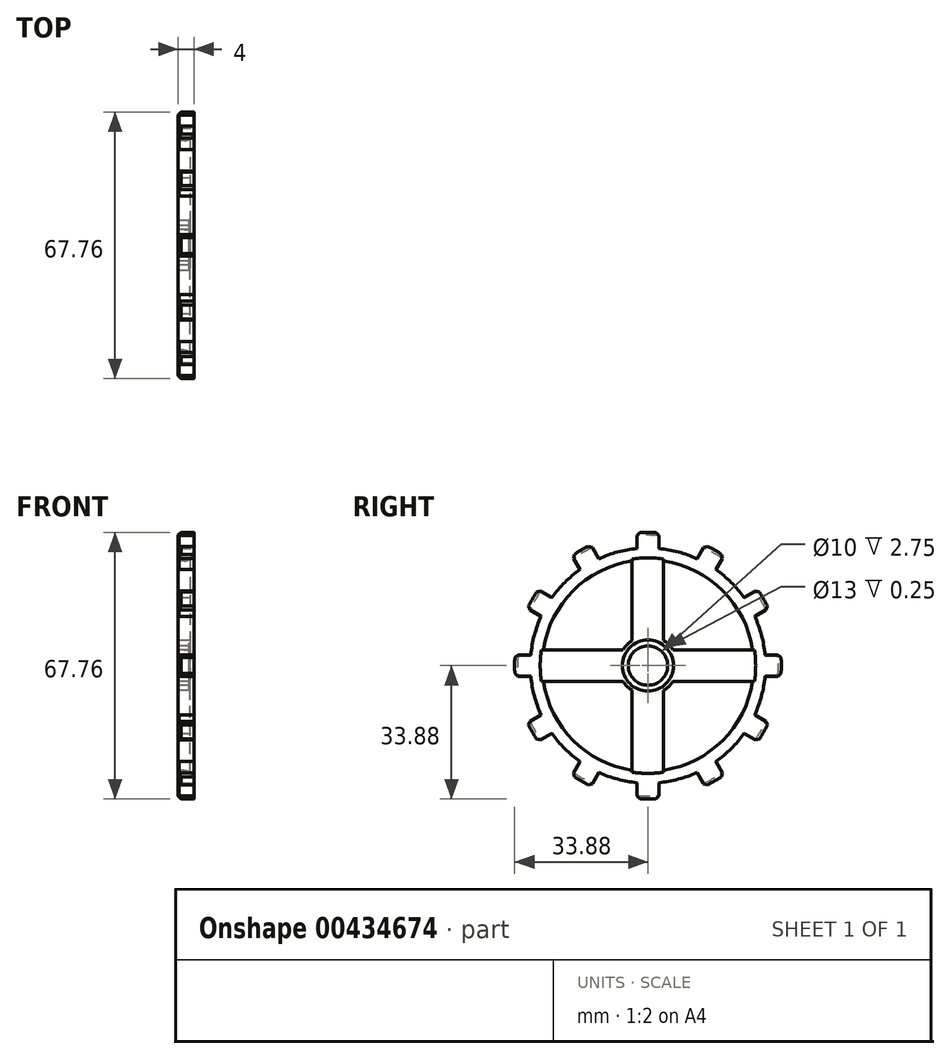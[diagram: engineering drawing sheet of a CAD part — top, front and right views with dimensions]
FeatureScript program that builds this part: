
annotation { "Feature Type Name" : "Feature", "Feature Type Description" : "" }
export const myFeature = defineFeature(function(context is Context, id is Id, definition is map)
    precondition{}
    {
        {
            assignVariable(context, id + "F0", {"name" : "Thickness", "anyValue" : 4});
        }
        {
            var Q0;
            Q0=qCreatedBy(makeId("Right.planeOp"),FACE);
            var sketch = newSketch(context, id + "F1", { "sketchPlane" : qUnion([Q0])});
            skLineSegment(sketch, "E0", {"start": v(-30, 0) * mm, "end": v(30, 0) * mm, "construction": true});
            skLineSegment(sketch, "E1", {"start": v(0, 30) * mm, "end": v(0, -30) * mm, "construction": true});
            skCircle(sketch, "E2", {"center": v(0, 0) * mm, "radius": 5 * mm});
            skCircle(sketch, "E3", {"center": v(0, 0) * mm, "radius": 6.5 * mm});
            skCircle(sketch, "E4", {"center": v(0, 0) * mm, "radius": 7.5 * mm});
            skSolve(sketch);
        }
        {
            var Q0;
            Q0=qCreatedBy(makeId("Right.planeOp"),FACE);
            var sketch = newSketch(context, id + "F2", { "sketchPlane" : qUnion([Q0])});
            skCircle(sketch, "E5", {"center": v(0, 0) * mm, "radius": 26.88 * mm});
            skCircle(sketch, "E6.0", {"center": v(0, 0) * mm, "radius": 29.88 * mm});
            skSolve(sketch);
        }
        {
            var Q0;
            Q0=qCreatedBy(makeId("Right.planeOp"),FACE);
            var sketch = newSketch(context, id + "F3", { "sketchPlane" : qUnion([Q0])});
            skCircle(sketch, "E7.0", {"center": v(0, 0) * mm, "radius": 26.88 * mm, "construction": true});
            skCircle(sketch, "E7.1", {"center": v(0, 0) * mm, "radius": 7.5 * mm, "construction": true});
            skLineSegment(sketch, "E7.2", {"start": v(-30, 0) * mm, "end": v(30, 0) * mm, "construction": true});
            skLineSegment(sketch, "E7.3", {"start": v(0, 30) * mm, "end": v(0, -30) * mm, "construction": true});
            skLineSegment(sketch, "E8", {"start": v(-4, 26.58) * mm, "end": v(-4, 6.34) * mm});
            skLineSegment(sketch, "E9.MirrorCS", {"start": v(4, 26.58) * mm, "end": v(4, 6.34) * mm});
            skArc(sketch, "E10", {"start": v(-4, 26.58) * mm, "mid": v(0, 26.88) * mm, "end": v(4, 26.58) * mm});
            skArc(sketch, "E11", {"start": v(-4, 6.34) * mm, "mid": v(0, 7.5) * mm, "end": v(4, 6.34) * mm});
            skArc(sketch, "E12.1.1", {"start": v(-6.34, -4) * mm, "mid": v(-7.5, 0) * mm, "end": v(-6.34, 4) * mm});
            skLineSegment(sketch, "E12.1.2", {"start": v(-26.58, -4) * mm, "end": v(-6.34, -4) * mm});
            skLineSegment(sketch, "E12.1.3", {"start": v(-26.58, 4) * mm, "end": v(-6.34, 4) * mm});
            skArc(sketch, "E12.1.4", {"start": v(-26.58, -4) * mm, "mid": v(-26.88, 0) * mm, "end": v(-26.58, 4) * mm});
            skArc(sketch, "E12.2.1", {"start": v(4, -6.34) * mm, "mid": v(0, -7.5) * mm, "end": v(-4, -6.34) * mm});
            skLineSegment(sketch, "E12.2.2", {"start": v(4, -26.58) * mm, "end": v(4, -6.34) * mm});
            skLineSegment(sketch, "E12.2.3", {"start": v(-4, -26.58) * mm, "end": v(-4, -6.34) * mm});
            skArc(sketch, "E12.2.4", {"start": v(4, -26.58) * mm, "mid": v(0, -26.88) * mm, "end": v(-4, -26.58) * mm});
            skArc(sketch, "E12.3.1", {"start": v(6.34, 4) * mm, "mid": v(7.5, 0) * mm, "end": v(6.34, -4) * mm});
            skLineSegment(sketch, "E12.3.2", {"start": v(26.58, 4) * mm, "end": v(6.34, 4) * mm});
            skLineSegment(sketch, "E12.3.3", {"start": v(26.58, -4) * mm, "end": v(6.34, -4) * mm});
            skArc(sketch, "E12.3.4", {"start": v(26.58, 4) * mm, "mid": v(26.88, 0) * mm, "end": v(26.58, -4) * mm});
            skSolve(sketch);
        }
        {
            var Q0;
            Q0=qCreatedBy(makeId("Right.planeOp"),FACE);
            var sketch = newSketch(context, id + "F4", { "sketchPlane" : qUnion([Q0])});
            skLineSegment(sketch, "E13.1", {"start": v(0, 30) * mm, "end": v(0, -30) * mm, "construction": true});
            skLineSegment(sketch, "E13.2", {"start": v(-30, 0) * mm, "end": v(30, 0) * mm, "construction": true});
            skLineSegment(sketch, "E14", {"start": v(-2.75, 29.75) * mm, "end": v(-2.75, 33.76) * mm});
            skLineSegment(sketch, "E15.MirrorCS", {"start": v(2.75, 29.75) * mm, "end": v(2.75, 33.76) * mm});
            skArc(sketch, "E16", {"start": v(2.75, 29.75) * mm, "mid": v(0, 29.88) * mm, "end": v(-2.75, 29.75) * mm});
            skArc(sketch, "E17.0", {"start": v(2.75, 33.76) * mm, "mid": v(0, 33.88) * mm, "end": v(-2.75, 33.76) * mm});
            skCircle(sketch, "E18.0", {"center": v(0, 0) * mm, "radius": 6.5 * mm});
            skArc(sketch, "E19.1.1", {"start": v(-12.5, 27.14) * mm, "mid": v(-14.94, 25.87) * mm, "end": v(-17.26, 24.39) * mm});
            skLineSegment(sketch, "E19.1.2", {"start": v(-17.26, 24.39) * mm, "end": v(-19.26, 27.86) * mm});
            skLineSegment(sketch, "E19.1.3", {"start": v(-12.5, 27.14) * mm, "end": v(-14.5, 30.61) * mm});
            skArc(sketch, "E19.1.4", {"start": v(-14.5, 30.61) * mm, "mid": v(-16.94, 29.34) * mm, "end": v(-19.26, 27.86) * mm});
            skArc(sketch, "E19.2.1", {"start": v(-24.39, 17.26) * mm, "mid": v(-25.87, 14.94) * mm, "end": v(-27.14, 12.5) * mm});
            skLineSegment(sketch, "E19.2.2", {"start": v(-27.14, 12.5) * mm, "end": v(-30.61, 14.5) * mm});
            skLineSegment(sketch, "E19.2.3", {"start": v(-24.39, 17.26) * mm, "end": v(-27.86, 19.26) * mm});
            skArc(sketch, "E19.2.4", {"start": v(-27.86, 19.26) * mm, "mid": v(-29.34, 16.94) * mm, "end": v(-30.61, 14.5) * mm});
            skArc(sketch, "E20.2.3.0", {"start": v(-29.75, 2.75) * mm, "mid": v(-29.88, 0) * mm, "end": v(-29.75, -2.75) * mm});
            skLineSegment(sketch, "E20.6.3.0", {"start": v(-29.75, -2.75) * mm, "end": v(-33.76, -2.75) * mm});
            skLineSegment(sketch, "E20.9.3.0", {"start": v(-29.75, 2.75) * mm, "end": v(-33.76, 2.75) * mm});
            skArc(sketch, "E20.12.3.0", {"start": v(-33.76, 2.75) * mm, "mid": v(-33.88, 0) * mm, "end": v(-33.76, -2.75) * mm});
            skArc(sketch, "E20.2.4.0", {"start": v(-27.14, -12.5) * mm, "mid": v(-25.87, -14.94) * mm, "end": v(-24.39, -17.26) * mm});
            skLineSegment(sketch, "E20.6.4.0", {"start": v(-24.39, -17.26) * mm, "end": v(-27.86, -19.26) * mm});
            skLineSegment(sketch, "E20.9.4.0", {"start": v(-27.14, -12.5) * mm, "end": v(-30.61, -14.5) * mm});
            skArc(sketch, "E20.12.4.0", {"start": v(-30.61, -14.5) * mm, "mid": v(-29.34, -16.94) * mm, "end": v(-27.86, -19.26) * mm});
            skArc(sketch, "E20.2.5.0", {"start": v(-17.26, -24.39) * mm, "mid": v(-14.94, -25.87) * mm, "end": v(-12.5, -27.14) * mm});
            skLineSegment(sketch, "E20.6.5.0", {"start": v(-12.5, -27.14) * mm, "end": v(-14.5, -30.61) * mm});
            skLineSegment(sketch, "E20.9.5.0", {"start": v(-17.26, -24.39) * mm, "end": v(-19.26, -27.86) * mm});
            skArc(sketch, "E20.12.5.0", {"start": v(-19.26, -27.86) * mm, "mid": v(-16.94, -29.34) * mm, "end": v(-14.5, -30.61) * mm});
            skArc(sketch, "E20.2.6.0", {"start": v(-2.75, -29.75) * mm, "mid": v(0, -29.88) * mm, "end": v(2.75, -29.75) * mm});
            skCircle(sketch, "E20.5.6.0", {"center": v(0, 0) * mm, "radius": 6.5 * mm, "construction": true});
            skLineSegment(sketch, "E20.6.6.0", {"start": v(2.75, -29.75) * mm, "end": v(2.75, -33.76) * mm});
            skLineSegment(sketch, "E20.9.6.0", {"start": v(-2.75, -29.75) * mm, "end": v(-2.75, -33.76) * mm});
            skArc(sketch, "E20.12.6.0", {"start": v(-2.75, -33.76) * mm, "mid": v(0, -33.88) * mm, "end": v(2.75, -33.76) * mm});
            skArc(sketch, "E20.2.7.0", {"start": v(12.5, -27.14) * mm, "mid": v(14.94, -25.87) * mm, "end": v(17.26, -24.39) * mm});
            skLineSegment(sketch, "E20.6.7.0", {"start": v(17.26, -24.39) * mm, "end": v(19.26, -27.86) * mm});
            skLineSegment(sketch, "E20.9.7.0", {"start": v(12.5, -27.14) * mm, "end": v(14.5, -30.61) * mm});
            skArc(sketch, "E20.12.7.0", {"start": v(14.5, -30.61) * mm, "mid": v(16.94, -29.34) * mm, "end": v(19.26, -27.86) * mm});
            skArc(sketch, "E20.2.8.0", {"start": v(24.39, -17.26) * mm, "mid": v(25.87, -14.94) * mm, "end": v(27.14, -12.5) * mm});
            skLineSegment(sketch, "E20.6.8.0", {"start": v(27.14, -12.5) * mm, "end": v(30.61, -14.5) * mm});
            skLineSegment(sketch, "E20.9.8.0", {"start": v(24.39, -17.26) * mm, "end": v(27.86, -19.26) * mm});
            skArc(sketch, "E20.12.8.0", {"start": v(27.86, -19.26) * mm, "mid": v(29.34, -16.94) * mm, "end": v(30.61, -14.5) * mm});
            skArc(sketch, "E20.2.9.0", {"start": v(29.75, -2.75) * mm, "mid": v(29.88, 0) * mm, "end": v(29.75, 2.75) * mm});
            skLineSegment(sketch, "E20.6.9.0", {"start": v(29.75, 2.75) * mm, "end": v(33.76, 2.75) * mm});
            skLineSegment(sketch, "E20.9.9.0", {"start": v(29.75, -2.75) * mm, "end": v(33.76, -2.75) * mm});
            skArc(sketch, "E20.12.9.0", {"start": v(33.76, -2.75) * mm, "mid": v(33.88, 0) * mm, "end": v(33.76, 2.75) * mm});
            skArc(sketch, "E20.2.10.0", {"start": v(27.14, 12.5) * mm, "mid": v(25.87, 14.94) * mm, "end": v(24.39, 17.26) * mm});
            skLineSegment(sketch, "E20.6.10.0", {"start": v(24.39, 17.26) * mm, "end": v(27.86, 19.26) * mm});
            skLineSegment(sketch, "E20.9.10.0", {"start": v(27.14, 12.5) * mm, "end": v(30.61, 14.5) * mm});
            skArc(sketch, "E20.12.10.0", {"start": v(30.61, 14.5) * mm, "mid": v(29.34, 16.94) * mm, "end": v(27.86, 19.26) * mm});
            skArc(sketch, "E20.2.11.0", {"start": v(17.26, 24.39) * mm, "mid": v(14.94, 25.87) * mm, "end": v(12.5, 27.14) * mm});
            skLineSegment(sketch, "E20.6.11.0", {"start": v(12.5, 27.14) * mm, "end": v(14.5, 30.61) * mm});
            skLineSegment(sketch, "E20.9.11.0", {"start": v(17.26, 24.39) * mm, "end": v(19.26, 27.86) * mm});
            skArc(sketch, "E20.12.11.0", {"start": v(19.26, 27.86) * mm, "mid": v(16.94, 29.34) * mm, "end": v(14.5, 30.61) * mm});
            skCircle(sketch, "E21.0", {"center": v(0, 0) * mm, "radius": 29.88 * mm, "construction": true});
            skSolve(sketch);
        }
        {
            var Q0;
            Q0=makeQuery(id+"F1.imprint","IMPRINT",FACE,{"disambiguationData":[TD([[makeQuery(id+"F1.imprint","IMPRINT",EDGE,{"derivedFrom":sQuery(id+"F1.wireOp",EDGE,"E2")}),-1.0]])]});
            extrude(context, id + "F5", {"entities" : qUnion([Q0]), "depth" : 2.5 * mm, "symmetric" : true});
        }
        {
            var Q0;
            Q0=makeQuery(id+"F1.imprint","IMPRINT",FACE,{"disambiguationData":[TD([[makeQuery(id+"F1.imprint","IMPRINT",EDGE,{"derivedFrom":sQuery(id+"F1.wireOp",EDGE,"E3")}),-1.0]])]});
            extrude(context, id + "F6", {"entities" : qUnion([Q0]), "operationType" : NewBodyOperationType.ADD, "depth" : 1.5 * mm});
        }
        {
            var Q0;
            Q0=makeQuery(id+"F1.imprint","IMPRINT",FACE,{"disambiguationData":[TD([[makeQuery(id+"F1.imprint","IMPRINT",EDGE,{"derivedFrom":sQuery(id+"F1.wireOp",EDGE,"E2")}),-1.0]])]});
            var Q1;
            Q1=makeQuery(id+"F1.imprint","IMPRINT",FACE,{"disambiguationData":[TD([[makeQuery(id+"F1.imprint","IMPRINT",EDGE,{"derivedFrom":sQuery(id+"F1.wireOp",EDGE,"E3")}),-1.0]])]});
            extrude(context, id + "F7", {"entities" : qUnion([Q0, Q1]), "operationType" : NewBodyOperationType.ADD, "oppositeDirection" : true, "depth" : 1.5 * mm});
        }
        {
            var Q0;
            Q0=qSketchRegion(id+"F3",true);
            extrude(context, id + "F8", {"entities" : qUnion([Q0]), "operationType" : NewBodyOperationType.ADD, "depth" : 3 * mm, "symmetric" : true});
        }
        {
            var Q0;
            Q0=makeQuery(id+"F2.imprint","IMPRINT",FACE,{"disambiguationData":[TD([[makeQuery(id+"F2.imprint","IMPRINT",EDGE,{"derivedFrom":sQuery(id+"F2.wireOp",EDGE,"E5")}),-1.0]])]});
            extrude(context, id + "F9", {"entities" : qUnion([Q0]), "operationType" : NewBodyOperationType.ADD, "depth" : (getVariable(context, 'Thickness') - 1.5) * mm, "hasSecondDirection" : true, "secondDirectionOppositeDirection" : true, "secondDirectionDepth" : 1.5 * mm});
        }
        {
            var Q0;
            Q0=makeQuery(id+"F4.imprint","IMPRINT",FACE,{"disambiguationData":[TD([[makeQuery(id+"F4.imprint","IMPRINT",EDGE,{"derivedFrom":sQuery(id+"F4.wireOp",EDGE,"E14")}),-1.0]])]});
            var Q1;
            Q1=makeQuery(id+"F4.imprint","IMPRINT",FACE,{"disambiguationData":[TD([[makeQuery(id+"F4.imprint","IMPRINT",EDGE,{"derivedFrom":sQuery(id+"F4.wireOp",EDGE,"E19.1.1")}),-1.0]])]});
            var Q2;
            Q2=makeQuery(id+"F4.imprint","IMPRINT",FACE,{"disambiguationData":[TD([[makeQuery(id+"F4.imprint","IMPRINT",EDGE,{"derivedFrom":sQuery(id+"F4.wireOp",EDGE,"E19.2.1")}),-1.0]])]});
            var Q3;
            Q3=makeQuery(id+"F4.imprint","IMPRINT",FACE,{"disambiguationData":[TD([[makeQuery(id+"F4.imprint","IMPRINT",EDGE,{"derivedFrom":sQuery(id+"F4.wireOp",EDGE,"E20.2.3.0")}),-1.0]])]});
            var Q4;
            Q4=makeQuery(id+"F4.imprint","IMPRINT",FACE,{"disambiguationData":[TD([[makeQuery(id+"F4.imprint","IMPRINT",EDGE,{"derivedFrom":sQuery(id+"F4.wireOp",EDGE,"E20.2.4.0")}),-1.0]])]});
            var Q5;
            Q5=makeQuery(id+"F4.imprint","IMPRINT",FACE,{"disambiguationData":[TD([[makeQuery(id+"F4.imprint","IMPRINT",EDGE,{"derivedFrom":sQuery(id+"F4.wireOp",EDGE,"E20.2.5.0")}),-1.0]])]});
            var Q6;
            Q6=makeQuery(id+"F4.imprint","IMPRINT",FACE,{"disambiguationData":[TD([[makeQuery(id+"F4.imprint","IMPRINT",EDGE,{"derivedFrom":sQuery(id+"F4.wireOp",EDGE,"E20.2.6.0")}),-1.0]])]});
            var Q7;
            Q7=makeQuery(id+"F4.imprint","IMPRINT",FACE,{"disambiguationData":[TD([[makeQuery(id+"F4.imprint","IMPRINT",EDGE,{"derivedFrom":sQuery(id+"F4.wireOp",EDGE,"E20.2.7.0")}),-1.0]])]});
            var Q8;
            Q8=makeQuery(id+"F4.imprint","IMPRINT",FACE,{"disambiguationData":[TD([[makeQuery(id+"F4.imprint","IMPRINT",EDGE,{"derivedFrom":sQuery(id+"F4.wireOp",EDGE,"E20.2.8.0")}),-1.0]])]});
            var Q9;
            Q9=makeQuery(id+"F4.imprint","IMPRINT",FACE,{"disambiguationData":[TD([[makeQuery(id+"F4.imprint","IMPRINT",EDGE,{"derivedFrom":sQuery(id+"F4.wireOp",EDGE,"E20.2.9.0")}),-1.0]])]});
            var Q10;
            Q10=makeQuery(id+"F4.imprint","IMPRINT",FACE,{"disambiguationData":[TD([[makeQuery(id+"F4.imprint","IMPRINT",EDGE,{"derivedFrom":sQuery(id+"F4.wireOp",EDGE,"E20.2.10.0")}),-1.0]])]});
            var Q11;
            Q11=makeQuery(id+"F4.imprint","IMPRINT",FACE,{"disambiguationData":[TD([[makeQuery(id+"F4.imprint","IMPRINT",EDGE,{"derivedFrom":sQuery(id+"F4.wireOp",EDGE,"E20.2.11.0")}),-1.0]])]});
            var Q12;
            Q12=makeQuery(id+"F9.opExtrude","CAP_FACE",FACE,{"disambiguationData":[OSD([sQuery(id+"F2.wireOp",EDGE,"E5"),sQuery(id+"F2.wireOp",EDGE,"E6.0")])],"isStart":false});
            extrude(context, id + "F10", {"entities" : qUnion([Q0, Q1, Q2, Q3, Q4, Q5, Q6, Q7, Q8, Q9, Q10, Q11]), "operationType" : NewBodyOperationType.ADD, "oppositeDirection" : true, "depth" : 1.5 * mm, "hasSecondDirection" : true, "secondDirectionBound" : BoundingType.UP_TO_SURFACE, "secondDirectionOppositeDirection" : false, "secondDirectionBoundEntityFace" : qUnion([Q12]), "secondDirectionDepth" : 25 * mm});
        }
        {
            var Q0;
            Q0=makeQuery(id+"F10.opExtrude","SWEPT_EDGE",EDGE,{"disambiguationData":[OSD([sQuery(id+"F4.wireOp",EDGE,"E20.9.9.0"),sQuery(id+"F4.wireOp",EDGE,"E20.12.9.0")])]});
            var Q1;
            Q1=makeQuery(id+"F10.opExtrude","SWEPT_EDGE",EDGE,{"disambiguationData":[OSD([sQuery(id+"F4.wireOp",EDGE,"E20.6.8.0"),sQuery(id+"F4.wireOp",EDGE,"E20.12.8.0")])]});
            var Q2;
            Q2=makeQuery(id+"F10.opExtrude","SWEPT_EDGE",EDGE,{"disambiguationData":[OSD([sQuery(id+"F4.wireOp",EDGE,"E20.9.8.0"),sQuery(id+"F4.wireOp",EDGE,"E20.12.8.0")])]});
            var Q3;
            Q3=makeQuery(id+"F10.opExtrude","SWEPT_EDGE",EDGE,{"disambiguationData":[OSD([sQuery(id+"F4.wireOp",EDGE,"E20.6.7.0"),sQuery(id+"F4.wireOp",EDGE,"E20.12.7.0")])]});
            var Q4;
            Q4=makeQuery(id+"F10.opExtrude","SWEPT_EDGE",EDGE,{"disambiguationData":[OSD([sQuery(id+"F4.wireOp",EDGE,"E20.9.7.0"),sQuery(id+"F4.wireOp",EDGE,"E20.12.7.0")])]});
            var Q5;
            Q5=makeQuery(id+"F10.opExtrude","SWEPT_EDGE",EDGE,{"disambiguationData":[OSD([sQuery(id+"F4.wireOp",EDGE,"E20.6.6.0"),sQuery(id+"F4.wireOp",EDGE,"E20.12.6.0")])]});
            var Q6;
            Q6=makeQuery(id+"F10.opExtrude","SWEPT_EDGE",EDGE,{"disambiguationData":[OSD([sQuery(id+"F4.wireOp",EDGE,"E20.9.6.0"),sQuery(id+"F4.wireOp",EDGE,"E20.12.6.0")])]});
            var Q7;
            Q7=makeQuery(id+"F10.opExtrude","SWEPT_EDGE",EDGE,{"disambiguationData":[OSD([sQuery(id+"F4.wireOp",EDGE,"E20.6.5.0"),sQuery(id+"F4.wireOp",EDGE,"E20.12.5.0")])]});
            var Q8;
            Q8=makeQuery(id+"F10.opExtrude","SWEPT_EDGE",EDGE,{"disambiguationData":[OSD([sQuery(id+"F4.wireOp",EDGE,"E20.9.5.0"),sQuery(id+"F4.wireOp",EDGE,"E20.12.5.0")])]});
            var Q9;
            Q9=makeQuery(id+"F10.opExtrude","SWEPT_EDGE",EDGE,{"disambiguationData":[OSD([sQuery(id+"F4.wireOp",EDGE,"E20.6.4.0"),sQuery(id+"F4.wireOp",EDGE,"E20.12.4.0")])]});
            var Q10;
            Q10=makeQuery(id+"F10.opExtrude","SWEPT_EDGE",EDGE,{"disambiguationData":[OSD([sQuery(id+"F4.wireOp",EDGE,"E20.9.4.0"),sQuery(id+"F4.wireOp",EDGE,"E20.12.4.0")])]});
            var Q11;
            Q11=makeQuery(id+"F10.opExtrude","SWEPT_EDGE",EDGE,{"disambiguationData":[OSD([sQuery(id+"F4.wireOp",EDGE,"E20.6.3.0"),sQuery(id+"F4.wireOp",EDGE,"E20.12.3.0")])]});
            var Q12;
            Q12=makeQuery(id+"F10.opExtrude","SWEPT_EDGE",EDGE,{"disambiguationData":[OSD([sQuery(id+"F4.wireOp",EDGE,"E20.9.3.0"),sQuery(id+"F4.wireOp",EDGE,"E20.12.3.0")])]});
            var Q13;
            Q13=makeQuery(id+"F10.opExtrude","SWEPT_EDGE",EDGE,{"disambiguationData":[OSD([sQuery(id+"F4.wireOp",EDGE,"E19.2.2"),sQuery(id+"F4.wireOp",EDGE,"E19.2.4")])]});
            var Q14;
            Q14=makeQuery(id+"F10.opExtrude","SWEPT_EDGE",EDGE,{"disambiguationData":[OSD([sQuery(id+"F4.wireOp",EDGE,"E19.1.2"),sQuery(id+"F4.wireOp",EDGE,"E19.1.4")])]});
            var Q15;
            Q15=makeQuery(id+"F10.opExtrude","SWEPT_EDGE",EDGE,{"disambiguationData":[OSD([sQuery(id+"F4.wireOp",EDGE,"E14"),sQuery(id+"F4.wireOp",EDGE,"E17.0")])]});
            var Q16;
            Q16=makeQuery(id+"F10.opExtrude","SWEPT_EDGE",EDGE,{"disambiguationData":[OSD([sQuery(id+"F4.wireOp",EDGE,"E20.9.11.0"),sQuery(id+"F4.wireOp",EDGE,"E20.12.11.0")])]});
            var Q17;
            Q17=makeQuery(id+"F10.opExtrude","SWEPT_EDGE",EDGE,{"disambiguationData":[OSD([sQuery(id+"F4.wireOp",EDGE,"E20.9.10.0"),sQuery(id+"F4.wireOp",EDGE,"E20.12.10.0")])]});
            var Q18;
            Q18=makeQuery(id+"F10.opExtrude","SWEPT_EDGE",EDGE,{"disambiguationData":[OSD([sQuery(id+"F4.wireOp",EDGE,"E20.6.9.0"),sQuery(id+"F4.wireOp",EDGE,"E20.12.9.0")])]});
            var Q19;
            Q19=makeQuery(id+"F10.opExtrude","SWEPT_EDGE",EDGE,{"disambiguationData":[OSD([sQuery(id+"F4.wireOp",EDGE,"E20.6.10.0"),sQuery(id+"F4.wireOp",EDGE,"E20.12.10.0")])]});
            var Q20;
            Q20=makeQuery(id+"F10.opExtrude","SWEPT_EDGE",EDGE,{"disambiguationData":[OSD([sQuery(id+"F4.wireOp",EDGE,"E20.6.11.0"),sQuery(id+"F4.wireOp",EDGE,"E20.12.11.0")])]});
            var Q21;
            Q21=makeQuery(id+"F10.opExtrude","SWEPT_EDGE",EDGE,{"disambiguationData":[OSD([sQuery(id+"F4.wireOp",EDGE,"E15.MirrorCS"),sQuery(id+"F4.wireOp",EDGE,"E17.0")])]});
            var Q22;
            Q22=makeQuery(id+"F10.opExtrude","SWEPT_EDGE",EDGE,{"disambiguationData":[OSD([sQuery(id+"F4.wireOp",EDGE,"E19.1.3"),sQuery(id+"F4.wireOp",EDGE,"E19.1.4")])]});
            var Q23;
            Q23=makeQuery(id+"F10.opExtrude","SWEPT_EDGE",EDGE,{"disambiguationData":[OSD([sQuery(id+"F4.wireOp",EDGE,"E19.2.3"),sQuery(id+"F4.wireOp",EDGE,"E19.2.4")])]});
            var Q24;
            Q24=makeQuery(id+"F10.opExtrude","TWEAK_EDGE",EDGE,{"derivedFrom":[makeQuery(id+"F9.opExtrude","CAP_FACE",FACE,{"disambiguationData":[OSD([sQuery(id+"F2.wireOp",EDGE,"E5"),sQuery(id+"F2.wireOp",EDGE,"E6.0")])],"isStart":false}),makeQuery(id+"F4.imprint","IMPRINT",EDGE,{"derivedFrom":sQuery(id+"F4.wireOp",EDGE,"E17.0")})]});
            var Q25;
            Q25=makeQuery(id+"F10.opExtrude","CAP_EDGE",EDGE,{"disambiguationData":[OSD([sQuery(id+"F4.wireOp",EDGE,"E17.0")])],"isStart":false});
            var Q26;
            Q26=makeQuery(id+"F10.opExtrude","CAP_EDGE",EDGE,{"disambiguationData":[OSD([sQuery(id+"F4.wireOp",EDGE,"E19.1.4")])],"isStart":false});
            var Q27;
            Q27=makeQuery(id+"F10.opExtrude","TWEAK_EDGE",EDGE,{"derivedFrom":[makeQuery(id+"F9.opExtrude","CAP_FACE",FACE,{"disambiguationData":[OSD([sQuery(id+"F2.wireOp",EDGE,"E5"),sQuery(id+"F2.wireOp",EDGE,"E6.0")])],"isStart":false}),makeQuery(id+"F4.imprint","IMPRINT",EDGE,{"derivedFrom":sQuery(id+"F4.wireOp",EDGE,"E19.1.4")})]});
            var Q28;
            Q28=makeQuery(id+"F10.opExtrude","CAP_EDGE",EDGE,{"disambiguationData":[OSD([sQuery(id+"F4.wireOp",EDGE,"E19.2.4")])],"isStart":false});
            var Q29;
            Q29=makeQuery(id+"F10.opExtrude","TWEAK_EDGE",EDGE,{"derivedFrom":[makeQuery(id+"F9.opExtrude","CAP_FACE",FACE,{"disambiguationData":[OSD([sQuery(id+"F2.wireOp",EDGE,"E5"),sQuery(id+"F2.wireOp",EDGE,"E6.0")])],"isStart":false}),makeQuery(id+"F4.imprint","IMPRINT",EDGE,{"derivedFrom":sQuery(id+"F4.wireOp",EDGE,"E19.2.4")})]});
            var Q30;
            Q30=makeQuery(id+"F10.opExtrude","TWEAK_EDGE",EDGE,{"derivedFrom":[makeQuery(id+"F9.opExtrude","CAP_FACE",FACE,{"disambiguationData":[OSD([sQuery(id+"F2.wireOp",EDGE,"E5"),sQuery(id+"F2.wireOp",EDGE,"E6.0")])],"isStart":false}),makeQuery(id+"F4.imprint","IMPRINT",EDGE,{"derivedFrom":sQuery(id+"F4.wireOp",EDGE,"E20.12.3.0")})]});
            var Q31;
            Q31=makeQuery(id+"F10.opExtrude","CAP_EDGE",EDGE,{"disambiguationData":[OSD([sQuery(id+"F4.wireOp",EDGE,"E20.12.3.0")])],"isStart":false});
            var Q32;
            Q32=makeQuery(id+"F10.opExtrude","TWEAK_EDGE",EDGE,{"derivedFrom":[makeQuery(id+"F9.opExtrude","CAP_FACE",FACE,{"disambiguationData":[OSD([sQuery(id+"F2.wireOp",EDGE,"E5"),sQuery(id+"F2.wireOp",EDGE,"E6.0")])],"isStart":false}),makeQuery(id+"F4.imprint","IMPRINT",EDGE,{"derivedFrom":sQuery(id+"F4.wireOp",EDGE,"E20.12.4.0")})]});
            var Q33;
            Q33=makeQuery(id+"F10.opExtrude","CAP_EDGE",EDGE,{"disambiguationData":[OSD([sQuery(id+"F4.wireOp",EDGE,"E20.12.4.0")])],"isStart":false});
            var Q34;
            Q34=makeQuery(id+"F10.opExtrude","CAP_EDGE",EDGE,{"disambiguationData":[OSD([sQuery(id+"F4.wireOp",EDGE,"E20.12.7.0")])],"isStart":false});
            var Q35;
            Q35=makeQuery(id+"F10.opExtrude","TWEAK_EDGE",EDGE,{"derivedFrom":[makeQuery(id+"F9.opExtrude","CAP_FACE",FACE,{"disambiguationData":[OSD([sQuery(id+"F2.wireOp",EDGE,"E5"),sQuery(id+"F2.wireOp",EDGE,"E6.0")])],"isStart":false}),makeQuery(id+"F4.imprint","IMPRINT",EDGE,{"derivedFrom":sQuery(id+"F4.wireOp",EDGE,"E20.12.7.0")})]});
            var Q36;
            Q36=makeQuery(id+"F10.opExtrude","TWEAK_EDGE",EDGE,{"derivedFrom":[makeQuery(id+"F9.opExtrude","CAP_FACE",FACE,{"disambiguationData":[OSD([sQuery(id+"F2.wireOp",EDGE,"E5"),sQuery(id+"F2.wireOp",EDGE,"E6.0")])],"isStart":false}),makeQuery(id+"F4.imprint","IMPRINT",EDGE,{"derivedFrom":sQuery(id+"F4.wireOp",EDGE,"E20.12.8.0")})]});
            var Q37;
            Q37=makeQuery(id+"F10.opExtrude","CAP_EDGE",EDGE,{"disambiguationData":[OSD([sQuery(id+"F4.wireOp",EDGE,"E20.12.8.0")])],"isStart":false});
            var Q38;
            Q38=makeQuery(id+"F10.opExtrude","TWEAK_EDGE",EDGE,{"derivedFrom":[makeQuery(id+"F9.opExtrude","CAP_FACE",FACE,{"disambiguationData":[OSD([sQuery(id+"F2.wireOp",EDGE,"E5"),sQuery(id+"F2.wireOp",EDGE,"E6.0")])],"isStart":false}),makeQuery(id+"F4.imprint","IMPRINT",EDGE,{"derivedFrom":sQuery(id+"F4.wireOp",EDGE,"E20.12.9.0")})]});
            var Q39;
            Q39=makeQuery(id+"F10.opExtrude","CAP_EDGE",EDGE,{"disambiguationData":[OSD([sQuery(id+"F4.wireOp",EDGE,"E20.12.9.0")])],"isStart":false});
            var Q40;
            Q40=makeQuery(id+"F10.opExtrude","CAP_EDGE",EDGE,{"disambiguationData":[OSD([sQuery(id+"F4.wireOp",EDGE,"E20.12.10.0")])],"isStart":false});
            var Q41;
            Q41=makeQuery(id+"F10.opExtrude","TWEAK_EDGE",EDGE,{"derivedFrom":[makeQuery(id+"F9.opExtrude","CAP_FACE",FACE,{"disambiguationData":[OSD([sQuery(id+"F2.wireOp",EDGE,"E5"),sQuery(id+"F2.wireOp",EDGE,"E6.0")])],"isStart":false}),makeQuery(id+"F4.imprint","IMPRINT",EDGE,{"derivedFrom":sQuery(id+"F4.wireOp",EDGE,"E20.12.10.0")})]});
            var Q42;
            Q42=makeQuery(id+"F10.opExtrude","TWEAK_EDGE",EDGE,{"derivedFrom":[makeQuery(id+"F9.opExtrude","CAP_FACE",FACE,{"disambiguationData":[OSD([sQuery(id+"F2.wireOp",EDGE,"E5"),sQuery(id+"F2.wireOp",EDGE,"E6.0")])],"isStart":false}),makeQuery(id+"F4.imprint","IMPRINT",EDGE,{"derivedFrom":sQuery(id+"F4.wireOp",EDGE,"E20.12.11.0")})]});
            var Q43;
            Q43=makeQuery(id+"F10.opExtrude","CAP_EDGE",EDGE,{"disambiguationData":[OSD([sQuery(id+"F4.wireOp",EDGE,"E20.12.11.0")])],"isStart":false});
            var Q44;
            Q44=makeQuery(id+"F10.opExtrude","TWEAK_EDGE",EDGE,{"derivedFrom":[makeQuery(id+"F9.opExtrude","CAP_FACE",FACE,{"disambiguationData":[OSD([sQuery(id+"F2.wireOp",EDGE,"E5"),sQuery(id+"F2.wireOp",EDGE,"E6.0")])],"isStart":false}),makeQuery(id+"F4.imprint","IMPRINT",EDGE,{"derivedFrom":sQuery(id+"F4.wireOp",EDGE,"E20.12.5.0")})]});
            var Q45;
            Q45=makeQuery(id+"F10.opExtrude","CAP_EDGE",EDGE,{"disambiguationData":[OSD([sQuery(id+"F4.wireOp",EDGE,"E20.12.5.0")])],"isStart":false});
            var Q46;
            Q46=makeQuery(id+"F10.opExtrude","CAP_EDGE",EDGE,{"disambiguationData":[OSD([sQuery(id+"F4.wireOp",EDGE,"E20.12.6.0")])],"isStart":false});
            var Q47;
            Q47=makeQuery(id+"F10.opExtrude","TWEAK_EDGE",EDGE,{"derivedFrom":[makeQuery(id+"F9.opExtrude","CAP_FACE",FACE,{"disambiguationData":[OSD([sQuery(id+"F2.wireOp",EDGE,"E5"),sQuery(id+"F2.wireOp",EDGE,"E6.0")])],"isStart":false}),makeQuery(id+"F4.imprint","IMPRINT",EDGE,{"derivedFrom":sQuery(id+"F4.wireOp",EDGE,"E20.12.6.0")})]});
            chamfer(context, id + "F11", {"entities" : qUnion([Q0, Q1, Q2, Q3, Q4, Q5, Q6, Q7, Q8, Q9, Q10, Q11, Q12, Q13, Q14, Q15, Q16, Q17, Q18, Q19, Q20, Q21, Q22, Q23, Q24, Q25, Q26, Q27, Q28, Q29, Q30, Q31, Q32, Q33, Q34, Q35, Q36, Q37, Q38, Q39, Q40, Q41, Q42, Q43, Q44, Q45, Q46, Q47]), "width" : 0.75 * mm, "tangentPropagation" : true});
        }
        {
            var Q0;
            Q0=makeQuery(id+"F10.opExtrude","TWEAK_EDGE",EDGE,{"derivedFrom":[makeQuery(id+"F9.opExtrude","CAP_FACE",FACE,{"disambiguationData":[OSD([sQuery(id+"F2.wireOp",EDGE,"E5"),sQuery(id+"F2.wireOp",EDGE,"E6.0")])],"isStart":false}),makeQuery(id+"F4.imprint","IMPRINT",EDGE,{"derivedFrom":sQuery(id+"F4.wireOp",EDGE,"E19.1.3")})]});
            var Q1;
            Q1=makeQuery(id+"F10.opExtrude","TWEAK_EDGE",EDGE,{"derivedFrom":[makeQuery(id+"F9.opExtrude","CAP_FACE",FACE,{"disambiguationData":[OSD([sQuery(id+"F2.wireOp",EDGE,"E5"),sQuery(id+"F2.wireOp",EDGE,"E6.0")])],"isStart":false}),makeQuery(id+"F4.imprint","IMPRINT",EDGE,{"derivedFrom":sQuery(id+"F4.wireOp",EDGE,"E19.1.2")})]});
            var Q2;
            Q2=makeQuery(id+"F10.opExtrude","TWEAK_EDGE",EDGE,{"derivedFrom":[makeQuery(id+"F9.opExtrude","CAP_FACE",FACE,{"disambiguationData":[OSD([sQuery(id+"F2.wireOp",EDGE,"E5"),sQuery(id+"F2.wireOp",EDGE,"E6.0")])],"isStart":false}),makeQuery(id+"F4.imprint","IMPRINT",EDGE,{"derivedFrom":sQuery(id+"F4.wireOp",EDGE,"E19.2.3")})]});
            var Q3;
            Q3=makeQuery(id+"F10.opExtrude","TWEAK_EDGE",EDGE,{"derivedFrom":[makeQuery(id+"F9.opExtrude","CAP_FACE",FACE,{"disambiguationData":[OSD([sQuery(id+"F2.wireOp",EDGE,"E5"),sQuery(id+"F2.wireOp",EDGE,"E6.0")])],"isStart":false}),makeQuery(id+"F4.imprint","IMPRINT",EDGE,{"derivedFrom":sQuery(id+"F4.wireOp",EDGE,"E19.2.2")})]});
            var Q4;
            Q4=makeQuery(id+"F10.opExtrude","TWEAK_EDGE",EDGE,{"derivedFrom":[makeQuery(id+"F9.opExtrude","CAP_FACE",FACE,{"disambiguationData":[OSD([sQuery(id+"F2.wireOp",EDGE,"E5"),sQuery(id+"F2.wireOp",EDGE,"E6.0")])],"isStart":false}),makeQuery(id+"F4.imprint","IMPRINT",EDGE,{"derivedFrom":sQuery(id+"F4.wireOp",EDGE,"E20.9.3.0")})]});
            var Q5;
            Q5=makeQuery(id+"F10.opExtrude","TWEAK_EDGE",EDGE,{"derivedFrom":[makeQuery(id+"F9.opExtrude","CAP_FACE",FACE,{"disambiguationData":[OSD([sQuery(id+"F2.wireOp",EDGE,"E5"),sQuery(id+"F2.wireOp",EDGE,"E6.0")])],"isStart":false}),makeQuery(id+"F4.imprint","IMPRINT",EDGE,{"derivedFrom":sQuery(id+"F4.wireOp",EDGE,"E20.6.3.0")})]});
            var Q6;
            Q6=makeQuery(id+"F10.opExtrude","TWEAK_EDGE",EDGE,{"derivedFrom":[makeQuery(id+"F9.opExtrude","CAP_FACE",FACE,{"disambiguationData":[OSD([sQuery(id+"F2.wireOp",EDGE,"E5"),sQuery(id+"F2.wireOp",EDGE,"E6.0")])],"isStart":false}),makeQuery(id+"F4.imprint","IMPRINT",EDGE,{"derivedFrom":sQuery(id+"F4.wireOp",EDGE,"E20.9.4.0")})]});
            var Q7;
            Q7=makeQuery(id+"F10.opExtrude","TWEAK_EDGE",EDGE,{"derivedFrom":[makeQuery(id+"F9.opExtrude","CAP_FACE",FACE,{"disambiguationData":[OSD([sQuery(id+"F2.wireOp",EDGE,"E5"),sQuery(id+"F2.wireOp",EDGE,"E6.0")])],"isStart":false}),makeQuery(id+"F4.imprint","IMPRINT",EDGE,{"derivedFrom":sQuery(id+"F4.wireOp",EDGE,"E14")})]});
            var Q8;
            Q8=makeQuery(id+"F10.opExtrude","TWEAK_EDGE",EDGE,{"derivedFrom":[makeQuery(id+"F9.opExtrude","CAP_FACE",FACE,{"disambiguationData":[OSD([sQuery(id+"F2.wireOp",EDGE,"E5"),sQuery(id+"F2.wireOp",EDGE,"E6.0")])],"isStart":false}),makeQuery(id+"F4.imprint","IMPRINT",EDGE,{"derivedFrom":sQuery(id+"F4.wireOp",EDGE,"E15.MirrorCS")})]});
            var Q9;
            Q9=makeQuery(id+"F10.opExtrude","TWEAK_EDGE",EDGE,{"derivedFrom":[makeQuery(id+"F9.opExtrude","CAP_FACE",FACE,{"disambiguationData":[OSD([sQuery(id+"F2.wireOp",EDGE,"E5"),sQuery(id+"F2.wireOp",EDGE,"E6.0")])],"isStart":false}),makeQuery(id+"F4.imprint","IMPRINT",EDGE,{"derivedFrom":sQuery(id+"F4.wireOp",EDGE,"E20.6.11.0")})]});
            var Q10;
            Q10=makeQuery(id+"F10.opExtrude","TWEAK_EDGE",EDGE,{"derivedFrom":[makeQuery(id+"F9.opExtrude","CAP_FACE",FACE,{"disambiguationData":[OSD([sQuery(id+"F2.wireOp",EDGE,"E5"),sQuery(id+"F2.wireOp",EDGE,"E6.0")])],"isStart":false}),makeQuery(id+"F4.imprint","IMPRINT",EDGE,{"derivedFrom":sQuery(id+"F4.wireOp",EDGE,"E20.9.11.0")})]});
            var Q11;
            Q11=makeQuery(id+"F10.opExtrude","TWEAK_EDGE",EDGE,{"derivedFrom":[makeQuery(id+"F9.opExtrude","CAP_FACE",FACE,{"disambiguationData":[OSD([sQuery(id+"F2.wireOp",EDGE,"E5"),sQuery(id+"F2.wireOp",EDGE,"E6.0")])],"isStart":false}),makeQuery(id+"F4.imprint","IMPRINT",EDGE,{"derivedFrom":sQuery(id+"F4.wireOp",EDGE,"E20.6.10.0")})]});
            var Q12;
            Q12=makeQuery(id+"F10.opExtrude","TWEAK_EDGE",EDGE,{"derivedFrom":[makeQuery(id+"F9.opExtrude","CAP_FACE",FACE,{"disambiguationData":[OSD([sQuery(id+"F2.wireOp",EDGE,"E5"),sQuery(id+"F2.wireOp",EDGE,"E6.0")])],"isStart":false}),makeQuery(id+"F4.imprint","IMPRINT",EDGE,{"derivedFrom":sQuery(id+"F4.wireOp",EDGE,"E20.9.10.0")})]});
            var Q13;
            Q13=makeQuery(id+"F10.opExtrude","TWEAK_EDGE",EDGE,{"derivedFrom":[makeQuery(id+"F9.opExtrude","CAP_FACE",FACE,{"disambiguationData":[OSD([sQuery(id+"F2.wireOp",EDGE,"E5"),sQuery(id+"F2.wireOp",EDGE,"E6.0")])],"isStart":false}),makeQuery(id+"F4.imprint","IMPRINT",EDGE,{"derivedFrom":sQuery(id+"F4.wireOp",EDGE,"E20.6.9.0")})]});
            var Q14;
            Q14=makeQuery(id+"F10.opExtrude","TWEAK_EDGE",EDGE,{"derivedFrom":[makeQuery(id+"F9.opExtrude","CAP_FACE",FACE,{"disambiguationData":[OSD([sQuery(id+"F2.wireOp",EDGE,"E5"),sQuery(id+"F2.wireOp",EDGE,"E6.0")])],"isStart":false}),makeQuery(id+"F4.imprint","IMPRINT",EDGE,{"derivedFrom":sQuery(id+"F4.wireOp",EDGE,"E20.9.9.0")})]});
            var Q15;
            Q15=makeQuery(id+"F10.opExtrude","TWEAK_EDGE",EDGE,{"derivedFrom":[makeQuery(id+"F9.opExtrude","CAP_FACE",FACE,{"disambiguationData":[OSD([sQuery(id+"F2.wireOp",EDGE,"E5"),sQuery(id+"F2.wireOp",EDGE,"E6.0")])],"isStart":false}),makeQuery(id+"F4.imprint","IMPRINT",EDGE,{"derivedFrom":sQuery(id+"F4.wireOp",EDGE,"E20.6.8.0")})]});
            var Q16;
            Q16=makeQuery(id+"F10.opExtrude","TWEAK_EDGE",EDGE,{"derivedFrom":[makeQuery(id+"F9.opExtrude","CAP_FACE",FACE,{"disambiguationData":[OSD([sQuery(id+"F2.wireOp",EDGE,"E5"),sQuery(id+"F2.wireOp",EDGE,"E6.0")])],"isStart":false}),makeQuery(id+"F4.imprint","IMPRINT",EDGE,{"derivedFrom":sQuery(id+"F4.wireOp",EDGE,"E20.9.8.0")})]});
            var Q17;
            Q17=makeQuery(id+"F10.opExtrude","TWEAK_EDGE",EDGE,{"derivedFrom":[makeQuery(id+"F9.opExtrude","CAP_FACE",FACE,{"disambiguationData":[OSD([sQuery(id+"F2.wireOp",EDGE,"E5"),sQuery(id+"F2.wireOp",EDGE,"E6.0")])],"isStart":false}),makeQuery(id+"F4.imprint","IMPRINT",EDGE,{"derivedFrom":sQuery(id+"F4.wireOp",EDGE,"E20.6.7.0")})]});
            var Q18;
            Q18=makeQuery(id+"F10.opExtrude","TWEAK_EDGE",EDGE,{"derivedFrom":[makeQuery(id+"F9.opExtrude","CAP_FACE",FACE,{"disambiguationData":[OSD([sQuery(id+"F2.wireOp",EDGE,"E5"),sQuery(id+"F2.wireOp",EDGE,"E6.0")])],"isStart":false}),makeQuery(id+"F4.imprint","IMPRINT",EDGE,{"derivedFrom":sQuery(id+"F4.wireOp",EDGE,"E20.9.7.0")})]});
            var Q19;
            Q19=makeQuery(id+"F10.opExtrude","TWEAK_EDGE",EDGE,{"derivedFrom":[makeQuery(id+"F9.opExtrude","CAP_FACE",FACE,{"disambiguationData":[OSD([sQuery(id+"F2.wireOp",EDGE,"E5"),sQuery(id+"F2.wireOp",EDGE,"E6.0")])],"isStart":false}),makeQuery(id+"F4.imprint","IMPRINT",EDGE,{"derivedFrom":sQuery(id+"F4.wireOp",EDGE,"E20.6.6.0")})]});
            var Q20;
            Q20=makeQuery(id+"F10.opExtrude","TWEAK_EDGE",EDGE,{"derivedFrom":[makeQuery(id+"F9.opExtrude","CAP_FACE",FACE,{"disambiguationData":[OSD([sQuery(id+"F2.wireOp",EDGE,"E5"),sQuery(id+"F2.wireOp",EDGE,"E6.0")])],"isStart":false}),makeQuery(id+"F4.imprint","IMPRINT",EDGE,{"derivedFrom":sQuery(id+"F4.wireOp",EDGE,"E20.9.6.0")})]});
            var Q21;
            Q21=makeQuery(id+"F10.opExtrude","TWEAK_EDGE",EDGE,{"derivedFrom":[makeQuery(id+"F9.opExtrude","CAP_FACE",FACE,{"disambiguationData":[OSD([sQuery(id+"F2.wireOp",EDGE,"E5"),sQuery(id+"F2.wireOp",EDGE,"E6.0")])],"isStart":false}),makeQuery(id+"F4.imprint","IMPRINT",EDGE,{"derivedFrom":sQuery(id+"F4.wireOp",EDGE,"E20.6.5.0")})]});
            var Q22;
            Q22=makeQuery(id+"F10.opExtrude","TWEAK_EDGE",EDGE,{"derivedFrom":[makeQuery(id+"F9.opExtrude","CAP_FACE",FACE,{"disambiguationData":[OSD([sQuery(id+"F2.wireOp",EDGE,"E5"),sQuery(id+"F2.wireOp",EDGE,"E6.0")])],"isStart":false}),makeQuery(id+"F4.imprint","IMPRINT",EDGE,{"derivedFrom":sQuery(id+"F4.wireOp",EDGE,"E20.9.5.0")})]});
            var Q23;
            Q23=makeQuery(id+"F10.opExtrude","TWEAK_EDGE",EDGE,{"derivedFrom":[makeQuery(id+"F9.opExtrude","CAP_FACE",FACE,{"disambiguationData":[OSD([sQuery(id+"F2.wireOp",EDGE,"E5"),sQuery(id+"F2.wireOp",EDGE,"E6.0")])],"isStart":false}),makeQuery(id+"F4.imprint","IMPRINT",EDGE,{"derivedFrom":sQuery(id+"F4.wireOp",EDGE,"E20.6.4.0")})]});
            var Q24;
            Q24=makeQuery(id+"F10.opExtrude","CAP_EDGE",EDGE,{"disambiguationData":[OSD([sQuery(id+"F4.wireOp",EDGE,"E20.9.11.0")])],"isStart":false});
            var Q25;
            Q25=makeQuery(id+"F10.opExtrude","CAP_EDGE",EDGE,{"disambiguationData":[OSD([sQuery(id+"F4.wireOp",EDGE,"E20.6.11.0")])],"isStart":false});
            var Q26;
            Q26=makeQuery(id+"F10.opExtrude","CAP_EDGE",EDGE,{"disambiguationData":[OSD([sQuery(id+"F4.wireOp",EDGE,"E20.6.10.0")])],"isStart":false});
            var Q27;
            Q27=makeQuery(id+"F10.opExtrude","CAP_EDGE",EDGE,{"disambiguationData":[OSD([sQuery(id+"F4.wireOp",EDGE,"E20.9.10.0")])],"isStart":false});
            var Q28;
            Q28=makeQuery(id+"F10.opExtrude","CAP_EDGE",EDGE,{"disambiguationData":[OSD([sQuery(id+"F4.wireOp",EDGE,"E15.MirrorCS")])],"isStart":false});
            var Q29;
            Q29=makeQuery(id+"F10.opExtrude","CAP_EDGE",EDGE,{"disambiguationData":[OSD([sQuery(id+"F4.wireOp",EDGE,"E20.6.9.0")])],"isStart":false});
            var Q30;
            Q30=makeQuery(id+"F10.opExtrude","CAP_EDGE",EDGE,{"disambiguationData":[OSD([sQuery(id+"F4.wireOp",EDGE,"E20.9.9.0")])],"isStart":false});
            var Q31;
            Q31=makeQuery(id+"F10.opExtrude","CAP_EDGE",EDGE,{"disambiguationData":[OSD([sQuery(id+"F4.wireOp",EDGE,"E20.9.4.0")])],"isStart":false});
            var Q32;
            Q32=makeQuery(id+"F10.opExtrude","CAP_EDGE",EDGE,{"disambiguationData":[OSD([sQuery(id+"F4.wireOp",EDGE,"E20.6.4.0")])],"isStart":false});
            var Q33;
            Q33=makeQuery(id+"F10.opExtrude","CAP_EDGE",EDGE,{"disambiguationData":[OSD([sQuery(id+"F4.wireOp",EDGE,"E20.9.5.0")])],"isStart":false});
            var Q34;
            Q34=makeQuery(id+"F10.opExtrude","CAP_EDGE",EDGE,{"disambiguationData":[OSD([sQuery(id+"F4.wireOp",EDGE,"E20.6.5.0")])],"isStart":false});
            var Q35;
            Q35=makeQuery(id+"F10.opExtrude","CAP_EDGE",EDGE,{"disambiguationData":[OSD([sQuery(id+"F4.wireOp",EDGE,"E20.9.6.0")])],"isStart":false});
            var Q36;
            Q36=makeQuery(id+"F10.opExtrude","CAP_EDGE",EDGE,{"disambiguationData":[OSD([sQuery(id+"F4.wireOp",EDGE,"E20.6.6.0")])],"isStart":false});
            var Q37;
            Q37=makeQuery(id+"F10.opExtrude","CAP_EDGE",EDGE,{"disambiguationData":[OSD([sQuery(id+"F4.wireOp",EDGE,"E20.9.3.0")])],"isStart":false});
            var Q38;
            Q38=makeQuery(id+"F10.opExtrude","CAP_EDGE",EDGE,{"disambiguationData":[OSD([sQuery(id+"F4.wireOp",EDGE,"E20.6.3.0")])],"isStart":false});
            var Q39;
            Q39=makeQuery(id+"F10.opExtrude","CAP_EDGE",EDGE,{"disambiguationData":[OSD([sQuery(id+"F4.wireOp",EDGE,"E20.6.8.0")])],"isStart":false});
            var Q40;
            Q40=makeQuery(id+"F10.opExtrude","CAP_EDGE",EDGE,{"disambiguationData":[OSD([sQuery(id+"F4.wireOp",EDGE,"E20.9.8.0")])],"isStart":false});
            var Q41;
            Q41=makeQuery(id+"F10.opExtrude","CAP_EDGE",EDGE,{"disambiguationData":[OSD([sQuery(id+"F4.wireOp",EDGE,"E20.6.7.0")])],"isStart":false});
            var Q42;
            Q42=makeQuery(id+"F10.opExtrude","CAP_EDGE",EDGE,{"disambiguationData":[OSD([sQuery(id+"F4.wireOp",EDGE,"E20.9.7.0")])],"isStart":false});
            var Q43;
            Q43=makeQuery(id+"F10.opExtrude","CAP_EDGE",EDGE,{"disambiguationData":[OSD([sQuery(id+"F4.wireOp",EDGE,"E14")])],"isStart":false});
            var Q44;
            Q44=makeQuery(id+"F10.opExtrude","CAP_EDGE",EDGE,{"disambiguationData":[OSD([sQuery(id+"F4.wireOp",EDGE,"E19.1.3")])],"isStart":false});
            var Q45;
            Q45=makeQuery(id+"F10.opExtrude","CAP_EDGE",EDGE,{"disambiguationData":[OSD([sQuery(id+"F4.wireOp",EDGE,"E19.1.2")])],"isStart":false});
            var Q46;
            Q46=makeQuery(id+"F10.opExtrude","CAP_EDGE",EDGE,{"disambiguationData":[OSD([sQuery(id+"F4.wireOp",EDGE,"E19.2.3")])],"isStart":false});
            var Q47;
            Q47=makeQuery(id+"F10.opExtrude","CAP_EDGE",EDGE,{"disambiguationData":[OSD([sQuery(id+"F4.wireOp",EDGE,"E19.2.2")])],"isStart":false});
            chamfer(context, id + "F12", {"entities" : qUnion([Q0, Q1, Q2, Q3, Q4, Q5, Q6, Q7, Q8, Q9, Q10, Q11, Q12, Q13, Q14, Q15, Q16, Q17, Q18, Q19, Q20, Q21, Q22, Q23, Q24, Q25, Q26, Q27, Q28, Q29, Q30, Q31, Q32, Q33, Q34, Q35, Q36, Q37, Q38, Q39, Q40, Q41, Q42, Q43, Q44, Q45, Q46, Q47]), "width" : 0.25 * mm, "tangentPropagation" : true});
        }
        {
            var Q0;
            Q0=makeQuery(id+"F9.opExtrude","CAP_EDGE",EDGE,{"disambiguationData":[OSD([sQuery(id+"F2.wireOp",EDGE,"E5")])],"isStart":false});
            var Q1;
            {var subQ0=sQuery(id+"F2.wireOp",EDGE,"E6.0");var subQ1=sQuery(id+"F2.wireOp",EDGE,"E5");Q1=makeQuery(id+"FG3cNUgKwzUiESX_1.opChamfer","BLEND_EDGE",EDGE,{"blendedFrom":[makeQuery(id+"F8.opExtrude","CAP_EDGE",EDGE,{"disambiguationData":[OSD([sQuery(id+"F8SyJBFYQLltGfZ_1.wireOp",EDGE,"233467de-cebd-4499-b968-40455db34306.1.3")])],"isStart":false}),makeQuery(id+"F10.boolean.opBoolean","MERGE",FACE,{"derivedFrom":[makeQuery(id+"F9.opExtrude","CAP_FACE",FACE,{"disambiguationData":[OSD([subQ1,subQ0])],"isStart":false}),makeQuery(id+"F10.opExtrude","CAP_FACE",FACE,{"disambiguationData":[OSD([subQ1,subQ0]),ownerDisambiguation([makeQuery(id+"F4.imprint","IMPRINT",EDGE,{"derivedFrom":sQuery(id+"F4.wireOp",EDGE,"E14")})])],"isStart":true}),makeQuery(id+"F10.opExtrude","CAP_FACE",FACE,{"disambiguationData":[OSD([subQ1,subQ0]),ownerDisambiguation([makeQuery(id+"F4.imprint","IMPRINT",EDGE,{"derivedFrom":sQuery(id+"F4.wireOp",EDGE,"E19.1.1")})])],"isStart":true}),makeQuery(id+"F10.opExtrude","CAP_FACE",FACE,{"disambiguationData":[OSD([subQ1,subQ0]),ownerDisambiguation([makeQuery(id+"F4.imprint","IMPRINT",EDGE,{"derivedFrom":sQuery(id+"F4.wireOp",EDGE,"E19.2.1")})])],"isStart":true}),makeQuery(id+"F10.opExtrude","CAP_FACE",FACE,{"disambiguationData":[OSD([subQ1,subQ0]),ownerDisambiguation([makeQuery(id+"F4.imprint","IMPRINT",EDGE,{"derivedFrom":sQuery(id+"F4.wireOp",EDGE,"E20.2.3.0")})])],"isStart":true}),makeQuery(id+"F10.opExtrude","CAP_FACE",FACE,{"disambiguationData":[OSD([subQ1,subQ0]),ownerDisambiguation([makeQuery(id+"F4.imprint","IMPRINT",EDGE,{"derivedFrom":sQuery(id+"F4.wireOp",EDGE,"E20.2.4.0")})])],"isStart":true}),makeQuery(id+"F10.opExtrude","CAP_FACE",FACE,{"disambiguationData":[OSD([subQ1,subQ0]),ownerDisambiguation([makeQuery(id+"F4.imprint","IMPRINT",EDGE,{"derivedFrom":sQuery(id+"F4.wireOp",EDGE,"E20.2.5.0")})])],"isStart":true}),makeQuery(id+"F10.opExtrude","CAP_FACE",FACE,{"disambiguationData":[OSD([subQ1,subQ0]),ownerDisambiguation([makeQuery(id+"F4.imprint","IMPRINT",EDGE,{"derivedFrom":sQuery(id+"F4.wireOp",EDGE,"E20.2.6.0")})])],"isStart":true}),makeQuery(id+"F10.opExtrude","CAP_FACE",FACE,{"disambiguationData":[OSD([subQ1,subQ0]),ownerDisambiguation([makeQuery(id+"F4.imprint","IMPRINT",EDGE,{"derivedFrom":sQuery(id+"F4.wireOp",EDGE,"E20.2.7.0")})])],"isStart":true}),makeQuery(id+"F10.opExtrude","CAP_FACE",FACE,{"disambiguationData":[OSD([subQ1,subQ0]),ownerDisambiguation([makeQuery(id+"F4.imprint","IMPRINT",EDGE,{"derivedFrom":sQuery(id+"F4.wireOp",EDGE,"E20.2.8.0")})])],"isStart":true}),makeQuery(id+"F10.opExtrude","CAP_FACE",FACE,{"disambiguationData":[OSD([subQ1,subQ0]),ownerDisambiguation([makeQuery(id+"F4.imprint","IMPRINT",EDGE,{"derivedFrom":sQuery(id+"F4.wireOp",EDGE,"E20.2.9.0")})])],"isStart":true}),makeQuery(id+"F10.opExtrude","CAP_FACE",FACE,{"disambiguationData":[OSD([subQ1,subQ0]),ownerDisambiguation([makeQuery(id+"F4.imprint","IMPRINT",EDGE,{"derivedFrom":sQuery(id+"F4.wireOp",EDGE,"E20.2.10.0")})])],"isStart":true}),makeQuery(id+"F10.opExtrude","CAP_FACE",FACE,{"disambiguationData":[OSD([subQ1,subQ0]),ownerDisambiguation([makeQuery(id+"F4.imprint","IMPRINT",EDGE,{"derivedFrom":sQuery(id+"F4.wireOp",EDGE,"E20.2.11.0")})])],"isStart":true})]})],"blendedInto":[makeQuery(id+"F10.boolean.opBoolean","MERGE",FACE,{"derivedFrom":[makeQuery(id+"F9.opExtrude","CAP_FACE",FACE,{"disambiguationData":[OSD([subQ1,subQ0])],"isStart":false}),makeQuery(id+"F10.opExtrude","CAP_FACE",FACE,{"disambiguationData":[OSD([subQ1,subQ0]),ownerDisambiguation([makeQuery(id+"F4.imprint","IMPRINT",EDGE,{"derivedFrom":sQuery(id+"F4.wireOp",EDGE,"E14")})])],"isStart":true}),makeQuery(id+"F10.opExtrude","CAP_FACE",FACE,{"disambiguationData":[OSD([subQ1,subQ0]),ownerDisambiguation([makeQuery(id+"F4.imprint","IMPRINT",EDGE,{"derivedFrom":sQuery(id+"F4.wireOp",EDGE,"E19.1.1")})])],"isStart":true}),makeQuery(id+"F10.opExtrude","CAP_FACE",FACE,{"disambiguationData":[OSD([subQ1,subQ0]),ownerDisambiguation([makeQuery(id+"F4.imprint","IMPRINT",EDGE,{"derivedFrom":sQuery(id+"F4.wireOp",EDGE,"E19.2.1")})])],"isStart":true}),makeQuery(id+"F10.opExtrude","CAP_FACE",FACE,{"disambiguationData":[OSD([subQ1,subQ0]),ownerDisambiguation([makeQuery(id+"F4.imprint","IMPRINT",EDGE,{"derivedFrom":sQuery(id+"F4.wireOp",EDGE,"E20.2.3.0")})])],"isStart":true}),makeQuery(id+"F10.opExtrude","CAP_FACE",FACE,{"disambiguationData":[OSD([subQ1,subQ0]),ownerDisambiguation([makeQuery(id+"F4.imprint","IMPRINT",EDGE,{"derivedFrom":sQuery(id+"F4.wireOp",EDGE,"E20.2.4.0")})])],"isStart":true}),makeQuery(id+"F10.opExtrude","CAP_FACE",FACE,{"disambiguationData":[OSD([subQ1,subQ0]),ownerDisambiguation([makeQuery(id+"F4.imprint","IMPRINT",EDGE,{"derivedFrom":sQuery(id+"F4.wireOp",EDGE,"E20.2.5.0")})])],"isStart":true}),makeQuery(id+"F10.opExtrude","CAP_FACE",FACE,{"disambiguationData":[OSD([subQ1,subQ0]),ownerDisambiguation([makeQuery(id+"F4.imprint","IMPRINT",EDGE,{"derivedFrom":sQuery(id+"F4.wireOp",EDGE,"E20.2.6.0")})])],"isStart":true}),makeQuery(id+"F10.opExtrude","CAP_FACE",FACE,{"disambiguationData":[OSD([subQ1,subQ0]),ownerDisambiguation([makeQuery(id+"F4.imprint","IMPRINT",EDGE,{"derivedFrom":sQuery(id+"F4.wireOp",EDGE,"E20.2.7.0")})])],"isStart":true}),makeQuery(id+"F10.opExtrude","CAP_FACE",FACE,{"disambiguationData":[OSD([subQ1,subQ0]),ownerDisambiguation([makeQuery(id+"F4.imprint","IMPRINT",EDGE,{"derivedFrom":sQuery(id+"F4.wireOp",EDGE,"E20.2.8.0")})])],"isStart":true}),makeQuery(id+"F10.opExtrude","CAP_FACE",FACE,{"disambiguationData":[OSD([subQ1,subQ0]),ownerDisambiguation([makeQuery(id+"F4.imprint","IMPRINT",EDGE,{"derivedFrom":sQuery(id+"F4.wireOp",EDGE,"E20.2.9.0")})])],"isStart":true}),makeQuery(id+"F10.opExtrude","CAP_FACE",FACE,{"disambiguationData":[OSD([subQ1,subQ0]),ownerDisambiguation([makeQuery(id+"F4.imprint","IMPRINT",EDGE,{"derivedFrom":sQuery(id+"F4.wireOp",EDGE,"E20.2.10.0")})])],"isStart":true}),makeQuery(id+"F10.opExtrude","CAP_FACE",FACE,{"disambiguationData":[OSD([subQ1,subQ0]),ownerDisambiguation([makeQuery(id+"F4.imprint","IMPRINT",EDGE,{"derivedFrom":sQuery(id+"F4.wireOp",EDGE,"E20.2.11.0")})])],"isStart":true})]})]});}
            var Q2;
            {var subQ0=sQuery(id+"F2.wireOp",EDGE,"E6.0");var subQ1=sQuery(id+"F2.wireOp",EDGE,"E5");Q2=makeQuery(id+"FG3cNUgKwzUiESX_1.opChamfer","BLEND_EDGE",EDGE,{"blendedFrom":[makeQuery(id+"F8.opExtrude","CAP_EDGE",EDGE,{"disambiguationData":[OSD([sQuery(id+"F8SyJBFYQLltGfZ_1.wireOp",EDGE,"c89d56af-5d7c-4f2b-b1cf-e0ae240ff1fd2")])],"isStart":false}),makeQuery(id+"F10.boolean.opBoolean","MERGE",FACE,{"derivedFrom":[makeQuery(id+"F9.opExtrude","CAP_FACE",FACE,{"disambiguationData":[OSD([subQ1,subQ0])],"isStart":false}),makeQuery(id+"F10.opExtrude","CAP_FACE",FACE,{"disambiguationData":[OSD([subQ1,subQ0]),ownerDisambiguation([makeQuery(id+"F4.imprint","IMPRINT",EDGE,{"derivedFrom":sQuery(id+"F4.wireOp",EDGE,"E14")})])],"isStart":true}),makeQuery(id+"F10.opExtrude","CAP_FACE",FACE,{"disambiguationData":[OSD([subQ1,subQ0]),ownerDisambiguation([makeQuery(id+"F4.imprint","IMPRINT",EDGE,{"derivedFrom":sQuery(id+"F4.wireOp",EDGE,"E19.1.1")})])],"isStart":true}),makeQuery(id+"F10.opExtrude","CAP_FACE",FACE,{"disambiguationData":[OSD([subQ1,subQ0]),ownerDisambiguation([makeQuery(id+"F4.imprint","IMPRINT",EDGE,{"derivedFrom":sQuery(id+"F4.wireOp",EDGE,"E19.2.1")})])],"isStart":true}),makeQuery(id+"F10.opExtrude","CAP_FACE",FACE,{"disambiguationData":[OSD([subQ1,subQ0]),ownerDisambiguation([makeQuery(id+"F4.imprint","IMPRINT",EDGE,{"derivedFrom":sQuery(id+"F4.wireOp",EDGE,"E20.2.3.0")})])],"isStart":true}),makeQuery(id+"F10.opExtrude","CAP_FACE",FACE,{"disambiguationData":[OSD([subQ1,subQ0]),ownerDisambiguation([makeQuery(id+"F4.imprint","IMPRINT",EDGE,{"derivedFrom":sQuery(id+"F4.wireOp",EDGE,"E20.2.4.0")})])],"isStart":true}),makeQuery(id+"F10.opExtrude","CAP_FACE",FACE,{"disambiguationData":[OSD([subQ1,subQ0]),ownerDisambiguation([makeQuery(id+"F4.imprint","IMPRINT",EDGE,{"derivedFrom":sQuery(id+"F4.wireOp",EDGE,"E20.2.5.0")})])],"isStart":true}),makeQuery(id+"F10.opExtrude","CAP_FACE",FACE,{"disambiguationData":[OSD([subQ1,subQ0]),ownerDisambiguation([makeQuery(id+"F4.imprint","IMPRINT",EDGE,{"derivedFrom":sQuery(id+"F4.wireOp",EDGE,"E20.2.6.0")})])],"isStart":true}),makeQuery(id+"F10.opExtrude","CAP_FACE",FACE,{"disambiguationData":[OSD([subQ1,subQ0]),ownerDisambiguation([makeQuery(id+"F4.imprint","IMPRINT",EDGE,{"derivedFrom":sQuery(id+"F4.wireOp",EDGE,"E20.2.7.0")})])],"isStart":true}),makeQuery(id+"F10.opExtrude","CAP_FACE",FACE,{"disambiguationData":[OSD([subQ1,subQ0]),ownerDisambiguation([makeQuery(id+"F4.imprint","IMPRINT",EDGE,{"derivedFrom":sQuery(id+"F4.wireOp",EDGE,"E20.2.8.0")})])],"isStart":true}),makeQuery(id+"F10.opExtrude","CAP_FACE",FACE,{"disambiguationData":[OSD([subQ1,subQ0]),ownerDisambiguation([makeQuery(id+"F4.imprint","IMPRINT",EDGE,{"derivedFrom":sQuery(id+"F4.wireOp",EDGE,"E20.2.9.0")})])],"isStart":true}),makeQuery(id+"F10.opExtrude","CAP_FACE",FACE,{"disambiguationData":[OSD([subQ1,subQ0]),ownerDisambiguation([makeQuery(id+"F4.imprint","IMPRINT",EDGE,{"derivedFrom":sQuery(id+"F4.wireOp",EDGE,"E20.2.10.0")})])],"isStart":true}),makeQuery(id+"F10.opExtrude","CAP_FACE",FACE,{"disambiguationData":[OSD([subQ1,subQ0]),ownerDisambiguation([makeQuery(id+"F4.imprint","IMPRINT",EDGE,{"derivedFrom":sQuery(id+"F4.wireOp",EDGE,"E20.2.11.0")})])],"isStart":true})]})],"blendedInto":[makeQuery(id+"F10.boolean.opBoolean","MERGE",FACE,{"derivedFrom":[makeQuery(id+"F9.opExtrude","CAP_FACE",FACE,{"disambiguationData":[OSD([subQ1,subQ0])],"isStart":false}),makeQuery(id+"F10.opExtrude","CAP_FACE",FACE,{"disambiguationData":[OSD([subQ1,subQ0]),ownerDisambiguation([makeQuery(id+"F4.imprint","IMPRINT",EDGE,{"derivedFrom":sQuery(id+"F4.wireOp",EDGE,"E14")})])],"isStart":true}),makeQuery(id+"F10.opExtrude","CAP_FACE",FACE,{"disambiguationData":[OSD([subQ1,subQ0]),ownerDisambiguation([makeQuery(id+"F4.imprint","IMPRINT",EDGE,{"derivedFrom":sQuery(id+"F4.wireOp",EDGE,"E19.1.1")})])],"isStart":true}),makeQuery(id+"F10.opExtrude","CAP_FACE",FACE,{"disambiguationData":[OSD([subQ1,subQ0]),ownerDisambiguation([makeQuery(id+"F4.imprint","IMPRINT",EDGE,{"derivedFrom":sQuery(id+"F4.wireOp",EDGE,"E19.2.1")})])],"isStart":true}),makeQuery(id+"F10.opExtrude","CAP_FACE",FACE,{"disambiguationData":[OSD([subQ1,subQ0]),ownerDisambiguation([makeQuery(id+"F4.imprint","IMPRINT",EDGE,{"derivedFrom":sQuery(id+"F4.wireOp",EDGE,"E20.2.3.0")})])],"isStart":true}),makeQuery(id+"F10.opExtrude","CAP_FACE",FACE,{"disambiguationData":[OSD([subQ1,subQ0]),ownerDisambiguation([makeQuery(id+"F4.imprint","IMPRINT",EDGE,{"derivedFrom":sQuery(id+"F4.wireOp",EDGE,"E20.2.4.0")})])],"isStart":true}),makeQuery(id+"F10.opExtrude","CAP_FACE",FACE,{"disambiguationData":[OSD([subQ1,subQ0]),ownerDisambiguation([makeQuery(id+"F4.imprint","IMPRINT",EDGE,{"derivedFrom":sQuery(id+"F4.wireOp",EDGE,"E20.2.5.0")})])],"isStart":true}),makeQuery(id+"F10.opExtrude","CAP_FACE",FACE,{"disambiguationData":[OSD([subQ1,subQ0]),ownerDisambiguation([makeQuery(id+"F4.imprint","IMPRINT",EDGE,{"derivedFrom":sQuery(id+"F4.wireOp",EDGE,"E20.2.6.0")})])],"isStart":true}),makeQuery(id+"F10.opExtrude","CAP_FACE",FACE,{"disambiguationData":[OSD([subQ1,subQ0]),ownerDisambiguation([makeQuery(id+"F4.imprint","IMPRINT",EDGE,{"derivedFrom":sQuery(id+"F4.wireOp",EDGE,"E20.2.7.0")})])],"isStart":true}),makeQuery(id+"F10.opExtrude","CAP_FACE",FACE,{"disambiguationData":[OSD([subQ1,subQ0]),ownerDisambiguation([makeQuery(id+"F4.imprint","IMPRINT",EDGE,{"derivedFrom":sQuery(id+"F4.wireOp",EDGE,"E20.2.8.0")})])],"isStart":true}),makeQuery(id+"F10.opExtrude","CAP_FACE",FACE,{"disambiguationData":[OSD([subQ1,subQ0]),ownerDisambiguation([makeQuery(id+"F4.imprint","IMPRINT",EDGE,{"derivedFrom":sQuery(id+"F4.wireOp",EDGE,"E20.2.9.0")})])],"isStart":true}),makeQuery(id+"F10.opExtrude","CAP_FACE",FACE,{"disambiguationData":[OSD([subQ1,subQ0]),ownerDisambiguation([makeQuery(id+"F4.imprint","IMPRINT",EDGE,{"derivedFrom":sQuery(id+"F4.wireOp",EDGE,"E20.2.10.0")})])],"isStart":true}),makeQuery(id+"F10.opExtrude","CAP_FACE",FACE,{"disambiguationData":[OSD([subQ1,subQ0]),ownerDisambiguation([makeQuery(id+"F4.imprint","IMPRINT",EDGE,{"derivedFrom":sQuery(id+"F4.wireOp",EDGE,"E20.2.11.0")})])],"isStart":true})]})]});}
            var Q3;
            Q3=makeQuery(id+"F9.opExtrude","CAP_EDGE",EDGE,{"disambiguationData":[OSD([sQuery(id+"F2.wireOp",EDGE,"E5")])],"isStart":false});
            var Q4;
            Q4=makeQuery(id+"F9.opExtrude","CAP_EDGE",EDGE,{"disambiguationData":[OSD([sQuery(id+"F2.wireOp",EDGE,"E5")])],"isStart":false});
            var Q5;
            {var subQ0=sQuery(id+"F2.wireOp",EDGE,"E6.0");var subQ1=sQuery(id+"F2.wireOp",EDGE,"E5");Q5=makeQuery(id+"FG3cNUgKwzUiESX_1.opChamfer","BLEND_EDGE",EDGE,{"blendedFrom":[makeQuery(id+"F8.opExtrude","CAP_EDGE",EDGE,{"disambiguationData":[OSD([sQuery(id+"F8SyJBFYQLltGfZ_1.wireOp",EDGE,"233467de-cebd-4499-b968-40455db34306.2.3")])],"isStart":false}),makeQuery(id+"F10.boolean.opBoolean","MERGE",FACE,{"derivedFrom":[makeQuery(id+"F9.opExtrude","CAP_FACE",FACE,{"disambiguationData":[OSD([subQ1,subQ0])],"isStart":false}),makeQuery(id+"F10.opExtrude","CAP_FACE",FACE,{"disambiguationData":[OSD([subQ1,subQ0]),ownerDisambiguation([makeQuery(id+"F4.imprint","IMPRINT",EDGE,{"derivedFrom":sQuery(id+"F4.wireOp",EDGE,"E14")})])],"isStart":true}),makeQuery(id+"F10.opExtrude","CAP_FACE",FACE,{"disambiguationData":[OSD([subQ1,subQ0]),ownerDisambiguation([makeQuery(id+"F4.imprint","IMPRINT",EDGE,{"derivedFrom":sQuery(id+"F4.wireOp",EDGE,"E19.1.1")})])],"isStart":true}),makeQuery(id+"F10.opExtrude","CAP_FACE",FACE,{"disambiguationData":[OSD([subQ1,subQ0]),ownerDisambiguation([makeQuery(id+"F4.imprint","IMPRINT",EDGE,{"derivedFrom":sQuery(id+"F4.wireOp",EDGE,"E19.2.1")})])],"isStart":true}),makeQuery(id+"F10.opExtrude","CAP_FACE",FACE,{"disambiguationData":[OSD([subQ1,subQ0]),ownerDisambiguation([makeQuery(id+"F4.imprint","IMPRINT",EDGE,{"derivedFrom":sQuery(id+"F4.wireOp",EDGE,"E20.2.3.0")})])],"isStart":true}),makeQuery(id+"F10.opExtrude","CAP_FACE",FACE,{"disambiguationData":[OSD([subQ1,subQ0]),ownerDisambiguation([makeQuery(id+"F4.imprint","IMPRINT",EDGE,{"derivedFrom":sQuery(id+"F4.wireOp",EDGE,"E20.2.4.0")})])],"isStart":true}),makeQuery(id+"F10.opExtrude","CAP_FACE",FACE,{"disambiguationData":[OSD([subQ1,subQ0]),ownerDisambiguation([makeQuery(id+"F4.imprint","IMPRINT",EDGE,{"derivedFrom":sQuery(id+"F4.wireOp",EDGE,"E20.2.5.0")})])],"isStart":true}),makeQuery(id+"F10.opExtrude","CAP_FACE",FACE,{"disambiguationData":[OSD([subQ1,subQ0]),ownerDisambiguation([makeQuery(id+"F4.imprint","IMPRINT",EDGE,{"derivedFrom":sQuery(id+"F4.wireOp",EDGE,"E20.2.6.0")})])],"isStart":true}),makeQuery(id+"F10.opExtrude","CAP_FACE",FACE,{"disambiguationData":[OSD([subQ1,subQ0]),ownerDisambiguation([makeQuery(id+"F4.imprint","IMPRINT",EDGE,{"derivedFrom":sQuery(id+"F4.wireOp",EDGE,"E20.2.7.0")})])],"isStart":true}),makeQuery(id+"F10.opExtrude","CAP_FACE",FACE,{"disambiguationData":[OSD([subQ1,subQ0]),ownerDisambiguation([makeQuery(id+"F4.imprint","IMPRINT",EDGE,{"derivedFrom":sQuery(id+"F4.wireOp",EDGE,"E20.2.8.0")})])],"isStart":true}),makeQuery(id+"F10.opExtrude","CAP_FACE",FACE,{"disambiguationData":[OSD([subQ1,subQ0]),ownerDisambiguation([makeQuery(id+"F4.imprint","IMPRINT",EDGE,{"derivedFrom":sQuery(id+"F4.wireOp",EDGE,"E20.2.9.0")})])],"isStart":true}),makeQuery(id+"F10.opExtrude","CAP_FACE",FACE,{"disambiguationData":[OSD([subQ1,subQ0]),ownerDisambiguation([makeQuery(id+"F4.imprint","IMPRINT",EDGE,{"derivedFrom":sQuery(id+"F4.wireOp",EDGE,"E20.2.10.0")})])],"isStart":true}),makeQuery(id+"F10.opExtrude","CAP_FACE",FACE,{"disambiguationData":[OSD([subQ1,subQ0]),ownerDisambiguation([makeQuery(id+"F4.imprint","IMPRINT",EDGE,{"derivedFrom":sQuery(id+"F4.wireOp",EDGE,"E20.2.11.0")})])],"isStart":true})]})],"blendedInto":[makeQuery(id+"F10.boolean.opBoolean","MERGE",FACE,{"derivedFrom":[makeQuery(id+"F9.opExtrude","CAP_FACE",FACE,{"disambiguationData":[OSD([subQ1,subQ0])],"isStart":false}),makeQuery(id+"F10.opExtrude","CAP_FACE",FACE,{"disambiguationData":[OSD([subQ1,subQ0]),ownerDisambiguation([makeQuery(id+"F4.imprint","IMPRINT",EDGE,{"derivedFrom":sQuery(id+"F4.wireOp",EDGE,"E14")})])],"isStart":true}),makeQuery(id+"F10.opExtrude","CAP_FACE",FACE,{"disambiguationData":[OSD([subQ1,subQ0]),ownerDisambiguation([makeQuery(id+"F4.imprint","IMPRINT",EDGE,{"derivedFrom":sQuery(id+"F4.wireOp",EDGE,"E19.1.1")})])],"isStart":true}),makeQuery(id+"F10.opExtrude","CAP_FACE",FACE,{"disambiguationData":[OSD([subQ1,subQ0]),ownerDisambiguation([makeQuery(id+"F4.imprint","IMPRINT",EDGE,{"derivedFrom":sQuery(id+"F4.wireOp",EDGE,"E19.2.1")})])],"isStart":true}),makeQuery(id+"F10.opExtrude","CAP_FACE",FACE,{"disambiguationData":[OSD([subQ1,subQ0]),ownerDisambiguation([makeQuery(id+"F4.imprint","IMPRINT",EDGE,{"derivedFrom":sQuery(id+"F4.wireOp",EDGE,"E20.2.3.0")})])],"isStart":true}),makeQuery(id+"F10.opExtrude","CAP_FACE",FACE,{"disambiguationData":[OSD([subQ1,subQ0]),ownerDisambiguation([makeQuery(id+"F4.imprint","IMPRINT",EDGE,{"derivedFrom":sQuery(id+"F4.wireOp",EDGE,"E20.2.4.0")})])],"isStart":true}),makeQuery(id+"F10.opExtrude","CAP_FACE",FACE,{"disambiguationData":[OSD([subQ1,subQ0]),ownerDisambiguation([makeQuery(id+"F4.imprint","IMPRINT",EDGE,{"derivedFrom":sQuery(id+"F4.wireOp",EDGE,"E20.2.5.0")})])],"isStart":true}),makeQuery(id+"F10.opExtrude","CAP_FACE",FACE,{"disambiguationData":[OSD([subQ1,subQ0]),ownerDisambiguation([makeQuery(id+"F4.imprint","IMPRINT",EDGE,{"derivedFrom":sQuery(id+"F4.wireOp",EDGE,"E20.2.6.0")})])],"isStart":true}),makeQuery(id+"F10.opExtrude","CAP_FACE",FACE,{"disambiguationData":[OSD([subQ1,subQ0]),ownerDisambiguation([makeQuery(id+"F4.imprint","IMPRINT",EDGE,{"derivedFrom":sQuery(id+"F4.wireOp",EDGE,"E20.2.7.0")})])],"isStart":true}),makeQuery(id+"F10.opExtrude","CAP_FACE",FACE,{"disambiguationData":[OSD([subQ1,subQ0]),ownerDisambiguation([makeQuery(id+"F4.imprint","IMPRINT",EDGE,{"derivedFrom":sQuery(id+"F4.wireOp",EDGE,"E20.2.8.0")})])],"isStart":true}),makeQuery(id+"F10.opExtrude","CAP_FACE",FACE,{"disambiguationData":[OSD([subQ1,subQ0]),ownerDisambiguation([makeQuery(id+"F4.imprint","IMPRINT",EDGE,{"derivedFrom":sQuery(id+"F4.wireOp",EDGE,"E20.2.9.0")})])],"isStart":true}),makeQuery(id+"F10.opExtrude","CAP_FACE",FACE,{"disambiguationData":[OSD([subQ1,subQ0]),ownerDisambiguation([makeQuery(id+"F4.imprint","IMPRINT",EDGE,{"derivedFrom":sQuery(id+"F4.wireOp",EDGE,"E20.2.10.0")})])],"isStart":true}),makeQuery(id+"F10.opExtrude","CAP_FACE",FACE,{"disambiguationData":[OSD([subQ1,subQ0]),ownerDisambiguation([makeQuery(id+"F4.imprint","IMPRINT",EDGE,{"derivedFrom":sQuery(id+"F4.wireOp",EDGE,"E20.2.11.0")})])],"isStart":true})]})]});}
            var Q6;
            Q6=makeQuery(id+"F9.opExtrude","CAP_EDGE",EDGE,{"disambiguationData":[OSD([sQuery(id+"F2.wireOp",EDGE,"E5")])],"isStart":false});
            var Q7;
            {var subQ0=sQuery(id+"F2.wireOp",EDGE,"E6.0");var subQ1=sQuery(id+"F2.wireOp",EDGE,"E5");Q7=makeQuery(id+"FG3cNUgKwzUiESX_1.opChamfer","BLEND_EDGE",EDGE,{"blendedFrom":[makeQuery(id+"F8.opExtrude","CAP_EDGE",EDGE,{"disambiguationData":[OSD([sQuery(id+"F8SyJBFYQLltGfZ_1.wireOp",EDGE,"233467de-cebd-4499-b968-40455db34306.3.3")])],"isStart":false}),makeQuery(id+"F10.boolean.opBoolean","MERGE",FACE,{"derivedFrom":[makeQuery(id+"F9.opExtrude","CAP_FACE",FACE,{"disambiguationData":[OSD([subQ1,subQ0])],"isStart":false}),makeQuery(id+"F10.opExtrude","CAP_FACE",FACE,{"disambiguationData":[OSD([subQ1,subQ0]),ownerDisambiguation([makeQuery(id+"F4.imprint","IMPRINT",EDGE,{"derivedFrom":sQuery(id+"F4.wireOp",EDGE,"E14")})])],"isStart":true}),makeQuery(id+"F10.opExtrude","CAP_FACE",FACE,{"disambiguationData":[OSD([subQ1,subQ0]),ownerDisambiguation([makeQuery(id+"F4.imprint","IMPRINT",EDGE,{"derivedFrom":sQuery(id+"F4.wireOp",EDGE,"E19.1.1")})])],"isStart":true}),makeQuery(id+"F10.opExtrude","CAP_FACE",FACE,{"disambiguationData":[OSD([subQ1,subQ0]),ownerDisambiguation([makeQuery(id+"F4.imprint","IMPRINT",EDGE,{"derivedFrom":sQuery(id+"F4.wireOp",EDGE,"E19.2.1")})])],"isStart":true}),makeQuery(id+"F10.opExtrude","CAP_FACE",FACE,{"disambiguationData":[OSD([subQ1,subQ0]),ownerDisambiguation([makeQuery(id+"F4.imprint","IMPRINT",EDGE,{"derivedFrom":sQuery(id+"F4.wireOp",EDGE,"E20.2.3.0")})])],"isStart":true}),makeQuery(id+"F10.opExtrude","CAP_FACE",FACE,{"disambiguationData":[OSD([subQ1,subQ0]),ownerDisambiguation([makeQuery(id+"F4.imprint","IMPRINT",EDGE,{"derivedFrom":sQuery(id+"F4.wireOp",EDGE,"E20.2.4.0")})])],"isStart":true}),makeQuery(id+"F10.opExtrude","CAP_FACE",FACE,{"disambiguationData":[OSD([subQ1,subQ0]),ownerDisambiguation([makeQuery(id+"F4.imprint","IMPRINT",EDGE,{"derivedFrom":sQuery(id+"F4.wireOp",EDGE,"E20.2.5.0")})])],"isStart":true}),makeQuery(id+"F10.opExtrude","CAP_FACE",FACE,{"disambiguationData":[OSD([subQ1,subQ0]),ownerDisambiguation([makeQuery(id+"F4.imprint","IMPRINT",EDGE,{"derivedFrom":sQuery(id+"F4.wireOp",EDGE,"E20.2.6.0")})])],"isStart":true}),makeQuery(id+"F10.opExtrude","CAP_FACE",FACE,{"disambiguationData":[OSD([subQ1,subQ0]),ownerDisambiguation([makeQuery(id+"F4.imprint","IMPRINT",EDGE,{"derivedFrom":sQuery(id+"F4.wireOp",EDGE,"E20.2.7.0")})])],"isStart":true}),makeQuery(id+"F10.opExtrude","CAP_FACE",FACE,{"disambiguationData":[OSD([subQ1,subQ0]),ownerDisambiguation([makeQuery(id+"F4.imprint","IMPRINT",EDGE,{"derivedFrom":sQuery(id+"F4.wireOp",EDGE,"E20.2.8.0")})])],"isStart":true}),makeQuery(id+"F10.opExtrude","CAP_FACE",FACE,{"disambiguationData":[OSD([subQ1,subQ0]),ownerDisambiguation([makeQuery(id+"F4.imprint","IMPRINT",EDGE,{"derivedFrom":sQuery(id+"F4.wireOp",EDGE,"E20.2.9.0")})])],"isStart":true}),makeQuery(id+"F10.opExtrude","CAP_FACE",FACE,{"disambiguationData":[OSD([subQ1,subQ0]),ownerDisambiguation([makeQuery(id+"F4.imprint","IMPRINT",EDGE,{"derivedFrom":sQuery(id+"F4.wireOp",EDGE,"E20.2.10.0")})])],"isStart":true}),makeQuery(id+"F10.opExtrude","CAP_FACE",FACE,{"disambiguationData":[OSD([subQ1,subQ0]),ownerDisambiguation([makeQuery(id+"F4.imprint","IMPRINT",EDGE,{"derivedFrom":sQuery(id+"F4.wireOp",EDGE,"E20.2.11.0")})])],"isStart":true})]})],"blendedInto":[makeQuery(id+"F10.boolean.opBoolean","MERGE",FACE,{"derivedFrom":[makeQuery(id+"F9.opExtrude","CAP_FACE",FACE,{"disambiguationData":[OSD([subQ1,subQ0])],"isStart":false}),makeQuery(id+"F10.opExtrude","CAP_FACE",FACE,{"disambiguationData":[OSD([subQ1,subQ0]),ownerDisambiguation([makeQuery(id+"F4.imprint","IMPRINT",EDGE,{"derivedFrom":sQuery(id+"F4.wireOp",EDGE,"E14")})])],"isStart":true}),makeQuery(id+"F10.opExtrude","CAP_FACE",FACE,{"disambiguationData":[OSD([subQ1,subQ0]),ownerDisambiguation([makeQuery(id+"F4.imprint","IMPRINT",EDGE,{"derivedFrom":sQuery(id+"F4.wireOp",EDGE,"E19.1.1")})])],"isStart":true}),makeQuery(id+"F10.opExtrude","CAP_FACE",FACE,{"disambiguationData":[OSD([subQ1,subQ0]),ownerDisambiguation([makeQuery(id+"F4.imprint","IMPRINT",EDGE,{"derivedFrom":sQuery(id+"F4.wireOp",EDGE,"E19.2.1")})])],"isStart":true}),makeQuery(id+"F10.opExtrude","CAP_FACE",FACE,{"disambiguationData":[OSD([subQ1,subQ0]),ownerDisambiguation([makeQuery(id+"F4.imprint","IMPRINT",EDGE,{"derivedFrom":sQuery(id+"F4.wireOp",EDGE,"E20.2.3.0")})])],"isStart":true}),makeQuery(id+"F10.opExtrude","CAP_FACE",FACE,{"disambiguationData":[OSD([subQ1,subQ0]),ownerDisambiguation([makeQuery(id+"F4.imprint","IMPRINT",EDGE,{"derivedFrom":sQuery(id+"F4.wireOp",EDGE,"E20.2.4.0")})])],"isStart":true}),makeQuery(id+"F10.opExtrude","CAP_FACE",FACE,{"disambiguationData":[OSD([subQ1,subQ0]),ownerDisambiguation([makeQuery(id+"F4.imprint","IMPRINT",EDGE,{"derivedFrom":sQuery(id+"F4.wireOp",EDGE,"E20.2.5.0")})])],"isStart":true}),makeQuery(id+"F10.opExtrude","CAP_FACE",FACE,{"disambiguationData":[OSD([subQ1,subQ0]),ownerDisambiguation([makeQuery(id+"F4.imprint","IMPRINT",EDGE,{"derivedFrom":sQuery(id+"F4.wireOp",EDGE,"E20.2.6.0")})])],"isStart":true}),makeQuery(id+"F10.opExtrude","CAP_FACE",FACE,{"disambiguationData":[OSD([subQ1,subQ0]),ownerDisambiguation([makeQuery(id+"F4.imprint","IMPRINT",EDGE,{"derivedFrom":sQuery(id+"F4.wireOp",EDGE,"E20.2.7.0")})])],"isStart":true}),makeQuery(id+"F10.opExtrude","CAP_FACE",FACE,{"disambiguationData":[OSD([subQ1,subQ0]),ownerDisambiguation([makeQuery(id+"F4.imprint","IMPRINT",EDGE,{"derivedFrom":sQuery(id+"F4.wireOp",EDGE,"E20.2.8.0")})])],"isStart":true}),makeQuery(id+"F10.opExtrude","CAP_FACE",FACE,{"disambiguationData":[OSD([subQ1,subQ0]),ownerDisambiguation([makeQuery(id+"F4.imprint","IMPRINT",EDGE,{"derivedFrom":sQuery(id+"F4.wireOp",EDGE,"E20.2.9.0")})])],"isStart":true}),makeQuery(id+"F10.opExtrude","CAP_FACE",FACE,{"disambiguationData":[OSD([subQ1,subQ0]),ownerDisambiguation([makeQuery(id+"F4.imprint","IMPRINT",EDGE,{"derivedFrom":sQuery(id+"F4.wireOp",EDGE,"E20.2.10.0")})])],"isStart":true}),makeQuery(id+"F10.opExtrude","CAP_FACE",FACE,{"disambiguationData":[OSD([subQ1,subQ0]),ownerDisambiguation([makeQuery(id+"F4.imprint","IMPRINT",EDGE,{"derivedFrom":sQuery(id+"F4.wireOp",EDGE,"E20.2.11.0")})])],"isStart":true})]})]});}
            fillet(context, id + "F13", {"entities" : qUnion([Q0, Q1, Q2, Q3, Q4, Q5, Q6, Q7]), "radius" : 2.5 * mm, "tangentPropagation" : true, "allowEdgeOverflow" : false});
        }
    });
